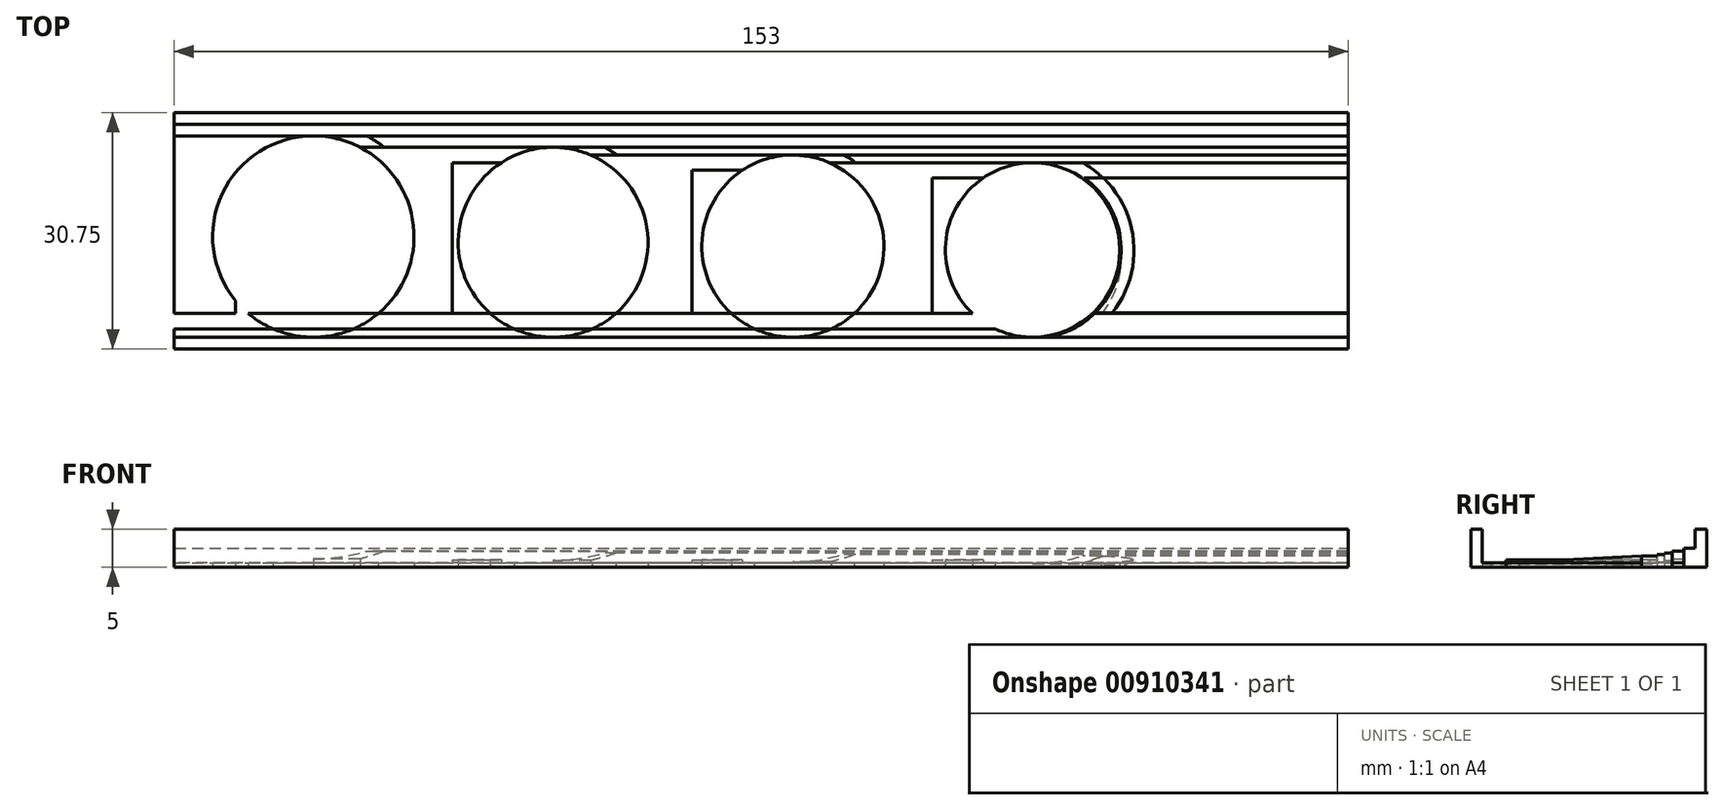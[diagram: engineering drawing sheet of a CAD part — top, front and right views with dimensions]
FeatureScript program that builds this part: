
annotation { "Feature Type Name" : "Feature", "Feature Type Description" : "" }
export const myFeature = defineFeature(function(context is Context, id is Id, definition is map)
    precondition{}
    {
        {
            var Q0;
            Q0=qCreatedBy(makeId("Top.planeOp"),FACE);
            var sketch = newSketch(context, id + "F0", { "sketchPlane" : qUnion([Q0])});
            skLineSegment(sketch, "E0.bottom", {"start": v(0, 0) * mm, "end": v(153, 0) * mm});
            skLineSegment(sketch, "E0.top", {"start": v(0, 29.25) * mm, "end": v(153, 29.25) * mm});
            skLineSegment(sketch, "E0.left", {"start": v(0, 0) * mm, "end": v(0, 29.25) * mm});
            skLineSegment(sketch, "E0.right", {"start": v(153, 0) * mm, "end": v(153, 29.25) * mm});
            skLineSegment(sketch, "E1", {"start": v(5, 0) * mm, "end": v(5, 29.25) * mm, "construction": true});
            skLineSegment(sketch, "E2", {"start": v(31.25, 0) * mm, "end": v(31.25, 29.25) * mm, "construction": true});
            skLineSegment(sketch, "E3", {"start": v(36.25, 29.25) * mm, "end": v(36.25, 0) * mm, "construction": true});
            skLineSegment(sketch, "E4", {"start": v(62.5, 0) * mm, "end": v(62.5, 29.25) * mm, "construction": true});
            skLineSegment(sketch, "E5", {"start": v(67.5, 29.25) * mm, "end": v(67.5, 0) * mm, "construction": true});
            skLineSegment(sketch, "E6", {"start": v(93.75, 29.25) * mm, "end": v(93.75, 0) * mm, "construction": true});
            skLineSegment(sketch, "E7", {"start": v(98.75, 29.25) * mm, "end": v(98.75, 0) * mm, "construction": true});
            skLineSegment(sketch, "E8", {"start": v(125, 29.25) * mm, "end": v(125, 0) * mm, "construction": true});
            skLineSegment(sketch, "E9", {"start": v(0, 1.1) * mm, "end": v(153, 1.1) * mm});
            skLineSegment(sketch, "E10", {"start": v(18.13, 0) * mm, "end": v(18.12, 29.25) * mm, "construction": true});
            skLineSegment(sketch, "E11", {"start": v(49.38, 0) * mm, "end": v(49.37, 29.25) * mm, "construction": true});
            skLineSegment(sketch, "E12", {"start": v(80.62, 29.25) * mm, "end": v(80.62, 0) * mm, "construction": true});
            skLineSegment(sketch, "E13", {"start": v(111.88, 0) * mm, "end": v(111.88, 29.25) * mm, "construction": true});
            skCircle(sketch, "E14", {"center": v(49.37, 12.38) * mm, "radius": 12.38 * mm});
            skCircle(sketch, "E15", {"center": v(80.62, 11.88) * mm, "radius": 11.88 * mm});
            skCircle(sketch, "E16", {"center": v(111.88, 11.38) * mm, "radius": 11.38 * mm});
            skCircle(sketch, "E17", {"center": v(18.12, 13.12) * mm, "radius": 13.12 * mm});
            skLineSegment(sketch, "E18", {"start": v(0, 26.25) * mm, "end": v(153, 26.25) * mm});
            skLineSegment(sketch, "E19", {"start": v(153, 24.75) * mm, "end": v(24.22, 24.75) * mm});
            skLineSegment(sketch, "E20", {"start": v(153, 23.75) * mm, "end": v(54.25, 23.75) * mm});
            skLineSegment(sketch, "E21", {"start": v(153, 22.75) * mm, "end": v(85.4, 22.75) * mm});
            skLineSegment(sketch, "E22", {"start": v(153, 20.75) * mm, "end": v(118.32, 20.75) * mm});
            skLineSegment(sketch, "E23", {"start": v(153, 27.75) * mm, "end": v(0, 27.75) * mm});
            skLineSegment(sketch, "E24", {"start": v(153, 0) * mm, "end": v(153, -1.5) * mm});
            skLineSegment(sketch, "E25", {"start": v(153, -1.5) * mm, "end": v(0, -1.5) * mm});
            skLineSegment(sketch, "E26", {"start": v(0, -1.5) * mm, "end": v(0, 0) * mm});
            skLineSegment(sketch, "E27", {"start": v(0, 3.1) * mm, "end": v(153, 3.1) * mm});
            skLineSegment(sketch, "E28.bottom", {"start": v(3, 3.1) * mm, "end": v(8, 3.1) * mm});
            skLineSegment(sketch, "E28.top", {"start": v(3, 26.25) * mm, "end": v(8, 26.25) * mm});
            skLineSegment(sketch, "E28.left", {"start": v(3, 3.1) * mm, "end": v(3, 26.25) * mm});
            skLineSegment(sketch, "E28.right", {"start": v(8, 3.1) * mm, "end": v(8, 26.25) * mm});
            skLineSegment(sketch, "E29.bottom", {"start": v(36.25, 3.1) * mm, "end": v(42.63, 3.1) * mm});
            skLineSegment(sketch, "E29.top", {"start": v(36.25, 22.75) * mm, "end": v(42.63, 22.75) * mm});
            skLineSegment(sketch, "E29.left", {"start": v(36.25, 3.1) * mm, "end": v(36.25, 22.75) * mm});
            skLineSegment(sketch, "E29.right", {"start": v(42.63, 3.1) * mm, "end": v(42.63, 22.75) * mm});
            skLineSegment(sketch, "E30.bottom", {"start": v(67.5, 3.1) * mm, "end": v(74.03, 3.1) * mm});
            skLineSegment(sketch, "E30.top", {"start": v(67.5, 21.75) * mm, "end": v(74.03, 21.75) * mm});
            skLineSegment(sketch, "E30.left", {"start": v(67.5, 3.1) * mm, "end": v(67.5, 21.75) * mm});
            skLineSegment(sketch, "E30.right", {"start": v(74.03, 3.1) * mm, "end": v(74.03, 21.75) * mm});
            skLineSegment(sketch, "E31.bottom", {"start": v(98.75, 3.1) * mm, "end": v(105.43, 3.1) * mm});
            skLineSegment(sketch, "E31.top", {"start": v(98.75, 20.75) * mm, "end": v(105.43, 20.75) * mm});
            skLineSegment(sketch, "E31.left", {"start": v(98.75, 3.1) * mm, "end": v(98.75, 20.75) * mm});
            skLineSegment(sketch, "E31.right", {"start": v(105.43, 3.1) * mm, "end": v(105.43, 20.75) * mm});
            skSolve(sketch);
        }
        {
            var Q0;
            {var subQ0=sQuery(id+"F0.wireOp",EDGE,"E14");var subQ1=sQuery(id+"F0.wireOp",EDGE,"E0.bottom");var subQ2=makeQuery(id+"F0.imprint","INTERSECT",VERTEX,{"derivedFrom":[subQ1,subQ0]});Q0=makeQuery(id+"F0.imprint","IMPRINT",FACE,{"disambiguationData":[TD([[makeQuery(id+"F0.imprint","IMPRINT",EDGE,{"disambiguationData":[TD([[subQ2,-1.0]])],"derivedFrom":subQ1}),1.0]])]});}
            var Q1;
            {var subQ0=sQuery(id+"F0.wireOp",EDGE,"E0.right");var subQ5=sQuery(id+"F0.wireOp",EDGE,"E9");var subQ6=makeQuery(id+"F0.imprint","INTERSECT",VERTEX,{"derivedFrom":[subQ0,subQ5]});Q1=makeQuery(id+"F0.imprint","IMPRINT",FACE,{"disambiguationData":[TD([[makeQuery(id+"F0.imprint","IMPRINT",EDGE,{"disambiguationData":[TD([[subQ6,1.0]])],"derivedFrom":subQ5}),-1.0]])]});}
            var Q2;
            {var subQ0=sQuery(id+"F0.wireOp",EDGE,"E17");var subQ1=sQuery(id+"F0.wireOp",EDGE,"E9");var subQ2=makeQuery(id+"F0.imprint","INTERSECT",VERTEX,{"disambiguationData":[OD(0.0)],"derivedFrom":[subQ1,subQ0]});Q2=makeQuery(id+"F0.imprint","IMPRINT",FACE,{"disambiguationData":[TD([[makeQuery(id+"F0.imprint","IMPRINT",EDGE,{"disambiguationData":[TD([[subQ2,-1.0]])],"derivedFrom":subQ1}),-1.0]])]});}
            var Q3;
            {var subQ0=sQuery(id+"F0.wireOp",EDGE,"E31.top");Q3=makeQuery(id+"F0.imprint","IMPRINT",FACE,{"disambiguationData":[TD([[makeQuery(id+"F0.imprint","IMPRINT",EDGE,{"derivedFrom":subQ0}),-1.0]])]});}
            var Q4;
            {var subQ1=sQuery(id+"F0.wireOp",EDGE,"E0.right");var subQ4=sQuery(id+"F0.wireOp",EDGE,"E20");var subQ5=makeQuery(id+"F0.imprint","INTERSECT",VERTEX,{"derivedFrom":[subQ1,subQ4]});Q4=makeQuery(id+"F0.imprint","IMPRINT",FACE,{"disambiguationData":[TD([[makeQuery(id+"F0.imprint","IMPRINT",EDGE,{"disambiguationData":[TD([[subQ5,1.0]])],"derivedFrom":subQ1}),1.0]])]});}
            var Q5;
            {var subQ1=sQuery(id+"F0.wireOp",EDGE,"E0.right");var subQ4=sQuery(id+"F0.wireOp",EDGE,"E19");var subQ5=makeQuery(id+"F0.imprint","INTERSECT",VERTEX,{"derivedFrom":[subQ1,subQ4]});Q5=makeQuery(id+"F0.imprint","IMPRINT",FACE,{"disambiguationData":[TD([[makeQuery(id+"F0.imprint","IMPRINT",EDGE,{"disambiguationData":[TD([[subQ5,1.0]])],"derivedFrom":subQ1}),1.0]])]});}
            var Q6;
            {var subQ0=sQuery(id+"F0.wireOp",EDGE,"E30.top");Q6=makeQuery(id+"F0.imprint","IMPRINT",FACE,{"disambiguationData":[TD([[makeQuery(id+"F0.imprint","IMPRINT",EDGE,{"derivedFrom":subQ0}),-1.0]])]});}
            var Q7;
            {var subQ3=sQuery(id+"F0.wireOp",EDGE,"E17");var subQ5=sQuery(id+"F0.wireOp",EDGE,"E9");var subQ6=makeQuery(id+"F0.imprint","INTERSECT",VERTEX,{"disambiguationData":[OD(1.0)],"derivedFrom":[subQ5,subQ3]});Q7=makeQuery(id+"F0.imprint","IMPRINT",FACE,{"disambiguationData":[TD([[makeQuery(id+"F0.imprint","IMPRINT",EDGE,{"disambiguationData":[TD([[subQ6,-1.0]])],"derivedFrom":subQ5}),1.0]])]});}
            var Q8;
            {var subQ5=sQuery(id+"F0.wireOp",EDGE,"E28.bottom");Q8=makeQuery(id+"F0.imprint","IMPRINT",FACE,{"disambiguationData":[TD([[makeQuery(id+"F0.imprint","IMPRINT",EDGE,{"derivedFrom":subQ5}),1.0]])]});}
            var Q9;
            {var subQ0=sQuery(id+"F0.wireOp",EDGE,"E16");var subQ1=sQuery(id+"F0.wireOp",EDGE,"E9");var subQ2=makeQuery(id+"F0.imprint","INTERSECT",VERTEX,{"disambiguationData":[OD(0.0)],"derivedFrom":[subQ1,subQ0]});Q9=makeQuery(id+"F0.imprint","IMPRINT",FACE,{"disambiguationData":[TD([[makeQuery(id+"F0.imprint","IMPRINT",EDGE,{"disambiguationData":[TD([[subQ2,-1.0]])],"derivedFrom":subQ1}),-1.0]])]});}
            var Q10;
            {var subQ6=sQuery(id+"F0.wireOp",EDGE,"E23");Q10=makeQuery(id+"F0.imprint","IMPRINT",FACE,{"disambiguationData":[TD([[makeQuery(id+"F0.imprint","IMPRINT",EDGE,{"derivedFrom":subQ6}),1.0]])]});}
            var Q11;
            {var subQ3=sQuery(id+"F0.wireOp",EDGE,"E22");Q11=makeQuery(id+"F0.imprint","IMPRINT",FACE,{"disambiguationData":[TD([[makeQuery(id+"F0.imprint","IMPRINT",EDGE,{"derivedFrom":subQ3}),-1.0]])]});}
            var Q12;
            {var subQ0=sQuery(id+"F0.wireOp",EDGE,"E22");Q12=makeQuery(id+"F0.imprint","IMPRINT",FACE,{"disambiguationData":[TD([[makeQuery(id+"F0.imprint","IMPRINT",EDGE,{"derivedFrom":subQ0}),1.0]])]});}
            var Q13;
            {var subQ5=sQuery(id+"F0.wireOp",EDGE,"E28.left");Q13=makeQuery(id+"F0.imprint","IMPRINT",FACE,{"disambiguationData":[TD([[makeQuery(id+"F0.imprint","IMPRINT",EDGE,{"derivedFrom":subQ5}),1.0]])]});}
            var Q14;
            {var subQ0=sQuery(id+"F0.wireOp",EDGE,"E0.left");var subQ5=sQuery(id+"F0.wireOp",EDGE,"E9");var subQ6=makeQuery(id+"F0.imprint","INTERSECT",VERTEX,{"derivedFrom":[subQ0,subQ5]});Q14=makeQuery(id+"F0.imprint","IMPRINT",FACE,{"disambiguationData":[TD([[makeQuery(id+"F0.imprint","IMPRINT",EDGE,{"disambiguationData":[TD([[subQ6,-1.0]])],"derivedFrom":subQ5}),-1.0]])]});}
            var Q15;
            {var subQ3=sQuery(id+"F0.wireOp",EDGE,"E14");var subQ6=sQuery(id+"F0.wireOp",EDGE,"E9");var subQ9=makeQuery(id+"F0.imprint","INTERSECT",VERTEX,{"disambiguationData":[OD(1.0)],"derivedFrom":[subQ6,subQ3]});Q15=makeQuery(id+"F0.imprint","IMPRINT",FACE,{"disambiguationData":[TD([[makeQuery(id+"F0.imprint","IMPRINT",EDGE,{"disambiguationData":[TD([[subQ9,-1.0]])],"derivedFrom":subQ6}),1.0]])]});}
            var Q16;
            {var subQ0=sQuery(id+"F0.wireOp",EDGE,"E17");var subQ1=sQuery(id+"F0.wireOp",EDGE,"E0.bottom");var subQ2=makeQuery(id+"F0.imprint","INTERSECT",VERTEX,{"derivedFrom":[subQ1,subQ0]});Q16=makeQuery(id+"F0.imprint","IMPRINT",FACE,{"disambiguationData":[TD([[makeQuery(id+"F0.imprint","IMPRINT",EDGE,{"disambiguationData":[TD([[subQ2,-1.0]])],"derivedFrom":subQ1}),1.0]])]});}
            var Q17;
            {var subQ5=sQuery(id+"F0.wireOp",EDGE,"E30.top");Q17=makeQuery(id+"F0.imprint","IMPRINT",FACE,{"disambiguationData":[TD([[makeQuery(id+"F0.imprint","IMPRINT",EDGE,{"derivedFrom":subQ5}),1.0]])]});}
            var Q18;
            {var subQ8=sQuery(id+"F0.wireOp",EDGE,"E29.top");Q18=makeQuery(id+"F0.imprint","IMPRINT",FACE,{"disambiguationData":[TD([[makeQuery(id+"F0.imprint","IMPRINT",EDGE,{"derivedFrom":subQ8}),1.0]])]});}
            var Q19;
            {var subQ8=sQuery(id+"F0.wireOp",EDGE,"E31.top");Q19=makeQuery(id+"F0.imprint","IMPRINT",FACE,{"disambiguationData":[TD([[makeQuery(id+"F0.imprint","IMPRINT",EDGE,{"derivedFrom":subQ8}),1.0]])]});}
            var Q20;
            {var subQ3=sQuery(id+"F0.wireOp",EDGE,"E28.bottom");Q20=makeQuery(id+"F0.imprint","IMPRINT",FACE,{"disambiguationData":[TD([[makeQuery(id+"F0.imprint","IMPRINT",EDGE,{"derivedFrom":subQ3}),-1.0]])]});}
            var Q21;
            {var subQ0=sQuery(id+"F0.wireOp",EDGE,"E14");var subQ1=sQuery(id+"F0.wireOp",EDGE,"E9");var subQ2=makeQuery(id+"F0.imprint","INTERSECT",VERTEX,{"disambiguationData":[OD(0.0)],"derivedFrom":[subQ1,subQ0]});Q21=makeQuery(id+"F0.imprint","IMPRINT",FACE,{"disambiguationData":[TD([[makeQuery(id+"F0.imprint","IMPRINT",EDGE,{"disambiguationData":[TD([[subQ2,-1.0]])],"derivedFrom":subQ1}),-1.0]])]});}
            var Q22;
            {var subQ1=sQuery(id+"F0.wireOp",EDGE,"E0.right");var subQ4=sQuery(id+"F0.wireOp",EDGE,"E18");var subQ5=makeQuery(id+"F0.imprint","INTERSECT",VERTEX,{"derivedFrom":[subQ1,subQ4]});Q22=makeQuery(id+"F0.imprint","IMPRINT",FACE,{"disambiguationData":[TD([[makeQuery(id+"F0.imprint","IMPRINT",EDGE,{"disambiguationData":[TD([[subQ5,1.0]])],"derivedFrom":subQ1}),1.0]])]});}
            var Q23;
            {var subQ0=sQuery(id+"F0.wireOp",EDGE,"E9");var subQ1=sQuery(id+"F0.wireOp",EDGE,"E0.right");var subQ2=makeQuery(id+"F0.imprint","INTERSECT",VERTEX,{"derivedFrom":[subQ1,subQ0]});Q23=makeQuery(id+"F0.imprint","IMPRINT",FACE,{"disambiguationData":[TD([[makeQuery(id+"F0.imprint","IMPRINT",EDGE,{"disambiguationData":[TD([[subQ2,-1.0]])],"derivedFrom":subQ1}),1.0]])]});}
            var Q24;
            {var subQ6=sQuery(id+"F0.wireOp",EDGE,"E24");Q24=makeQuery(id+"F0.imprint","IMPRINT",FACE,{"disambiguationData":[TD([[makeQuery(id+"F0.imprint","IMPRINT",EDGE,{"derivedFrom":subQ6}),-1.0]])]});}
            var Q25;
            {var subQ3=sQuery(id+"F0.wireOp",EDGE,"E15");var subQ6=sQuery(id+"F0.wireOp",EDGE,"E9");var subQ9=makeQuery(id+"F0.imprint","INTERSECT",VERTEX,{"disambiguationData":[OD(1.0)],"derivedFrom":[subQ6,subQ3]});Q25=makeQuery(id+"F0.imprint","IMPRINT",FACE,{"disambiguationData":[TD([[makeQuery(id+"F0.imprint","IMPRINT",EDGE,{"disambiguationData":[TD([[subQ9,-1.0]])],"derivedFrom":subQ6}),1.0]])]});}
            var Q26;
            {var subQ0=sQuery(id+"F0.wireOp",EDGE,"E0.top");Q26=makeQuery(id+"F0.imprint","IMPRINT",FACE,{"disambiguationData":[TD([[makeQuery(id+"F0.imprint","IMPRINT",EDGE,{"derivedFrom":subQ0}),-1.0]])]});}
            var Q27;
            {var subQ0=sQuery(id+"F0.wireOp",EDGE,"E29.top");Q27=makeQuery(id+"F0.imprint","IMPRINT",FACE,{"disambiguationData":[TD([[makeQuery(id+"F0.imprint","IMPRINT",EDGE,{"derivedFrom":subQ0}),-1.0]])]});}
            var Q28;
            {var subQ0=sQuery(id+"F0.wireOp",EDGE,"E15");var subQ1=sQuery(id+"F0.wireOp",EDGE,"E9");var subQ2=makeQuery(id+"F0.imprint","INTERSECT",VERTEX,{"disambiguationData":[OD(0.0)],"derivedFrom":[subQ1,subQ0]});Q28=makeQuery(id+"F0.imprint","IMPRINT",FACE,{"disambiguationData":[TD([[makeQuery(id+"F0.imprint","IMPRINT",EDGE,{"disambiguationData":[TD([[subQ2,-1.0]])],"derivedFrom":subQ1}),-1.0]])]});}
            var Q29;
            {var subQ0=sQuery(id+"F0.wireOp",EDGE,"E18");var subQ1=sQuery(id+"F0.wireOp",EDGE,"E17");var subQ2=makeQuery(id+"F0.imprint","INTERSECT",VERTEX,{"derivedFrom":[subQ1,subQ0]});Q29=makeQuery(id+"F0.imprint","IMPRINT",FACE,{"disambiguationData":[TD([[makeQuery(id+"F0.imprint","IMPRINT",EDGE,{"disambiguationData":[TD([[subQ2,-1.0]])],"derivedFrom":subQ1}),-1.0]])]});}
            var Q30;
            {var subQ0=sQuery(id+"F0.wireOp",EDGE,"E15");var subQ1=sQuery(id+"F0.wireOp",EDGE,"E0.bottom");var subQ2=makeQuery(id+"F0.imprint","INTERSECT",VERTEX,{"derivedFrom":[subQ1,subQ0]});Q30=makeQuery(id+"F0.imprint","IMPRINT",FACE,{"disambiguationData":[TD([[makeQuery(id+"F0.imprint","IMPRINT",EDGE,{"disambiguationData":[TD([[subQ2,-1.0]])],"derivedFrom":subQ1}),1.0]])]});}
            var Q31;
            {var subQ0=sQuery(id+"F0.wireOp",EDGE,"E28.right");var subQ1=sQuery(id+"F0.wireOp",EDGE,"E17");var subQ2=makeQuery(id+"F0.imprint","INTERSECT",VERTEX,{"disambiguationData":[OD(1.0)],"derivedFrom":[subQ1,subQ0]});Q31=makeQuery(id+"F0.imprint","IMPRINT",FACE,{"disambiguationData":[TD([[makeQuery(id+"F0.imprint","IMPRINT",EDGE,{"disambiguationData":[TD([[subQ2,-1.0]])],"derivedFrom":subQ1}),-1.0]])]});}
            extrude(context, id + "F1", {"entities" : qUnion([Q0, Q1, Q2, Q3, Q4, Q5, Q6, Q7, Q8, Q9, Q10, Q11, Q12, Q13, Q14, Q15, Q16, Q17, Q18, Q19, Q20, Q21, Q22, Q23, Q24, Q25, Q26, Q27, Q28, Q29, Q30, Q31]), "depth" : 0.6 * mm, "offsetDistance" : 25 * mm});
        }
        {
            var Q0;
            {var subQ6=sQuery(id+"F0.wireOp",EDGE,"E23");Q0=makeQuery(id+"F0.imprint","IMPRINT",FACE,{"disambiguationData":[TD([[makeQuery(id+"F0.imprint","IMPRINT",EDGE,{"derivedFrom":subQ6}),1.0]])]});}
            extrude(context, id + "F2", {"entities" : qUnion([Q0]), "depth" : 2.5 * mm, "offsetDistance" : 25 * mm});
        }
        {
            var Q0;
            {var subQ1=sQuery(id+"F0.wireOp",EDGE,"E0.right");var subQ4=sQuery(id+"F0.wireOp",EDGE,"E18");var subQ5=makeQuery(id+"F0.imprint","INTERSECT",VERTEX,{"derivedFrom":[subQ1,subQ4]});Q0=makeQuery(id+"F0.imprint","IMPRINT",FACE,{"disambiguationData":[TD([[makeQuery(id+"F0.imprint","IMPRINT",EDGE,{"disambiguationData":[TD([[subQ5,1.0]])],"derivedFrom":subQ1}),1.0]])]});}
            extrude(context, id + "F3", {"entities" : qUnion([Q0]), "depth" : 2.1 * mm, "offsetDistance" : 25 * mm});
        }
        {
            var Q0;
            {var subQ1=sQuery(id+"F0.wireOp",EDGE,"E0.right");var subQ4=sQuery(id+"F0.wireOp",EDGE,"E19");var subQ5=makeQuery(id+"F0.imprint","INTERSECT",VERTEX,{"derivedFrom":[subQ1,subQ4]});Q0=makeQuery(id+"F0.imprint","IMPRINT",FACE,{"disambiguationData":[TD([[makeQuery(id+"F0.imprint","IMPRINT",EDGE,{"disambiguationData":[TD([[subQ5,1.0]])],"derivedFrom":subQ1}),1.0]])]});}
            extrude(context, id + "F4", {"entities" : qUnion([Q0]), "depth" : 1.9 * mm, "offsetDistance" : 25 * mm});
        }
        {
            var Q0;
            {var subQ1=sQuery(id+"F0.wireOp",EDGE,"E0.right");var subQ4=sQuery(id+"F0.wireOp",EDGE,"E20");var subQ5=makeQuery(id+"F0.imprint","INTERSECT",VERTEX,{"derivedFrom":[subQ1,subQ4]});Q0=makeQuery(id+"F0.imprint","IMPRINT",FACE,{"disambiguationData":[TD([[makeQuery(id+"F0.imprint","IMPRINT",EDGE,{"disambiguationData":[TD([[subQ5,1.0]])],"derivedFrom":subQ1}),1.0]])]});}
            extrude(context, id + "F5", {"entities" : qUnion([Q0]), "operationType" : NewBodyOperationType.ADD, "depth" : 1.7 * mm, "offsetDistance" : 25 * mm});
        }
        {
            var Q0;
            {var subQ3=sQuery(id+"F0.wireOp",EDGE,"E22");Q0=makeQuery(id+"F0.imprint","IMPRINT",FACE,{"disambiguationData":[TD([[makeQuery(id+"F0.imprint","IMPRINT",EDGE,{"derivedFrom":subQ3}),-1.0]])]});}
            extrude(context, id + "F6", {"entities" : qUnion([Q0]), "operationType" : NewBodyOperationType.ADD, "depth" : 1.5 * mm, "offsetDistance" : 25 * mm});
        }
        {
            var Q0;
            {var subQ5=sQuery(id+"F0.wireOp",EDGE,"E28.bottom");Q0=makeQuery(id+"F0.imprint","IMPRINT",FACE,{"disambiguationData":[TD([[makeQuery(id+"F0.imprint","IMPRINT",EDGE,{"derivedFrom":subQ5}),1.0]])]});}
            var Q1;
            {var subQ0=sQuery(id+"F0.wireOp",EDGE,"E29.top");Q1=makeQuery(id+"F0.imprint","IMPRINT",FACE,{"disambiguationData":[TD([[makeQuery(id+"F0.imprint","IMPRINT",EDGE,{"derivedFrom":subQ0}),-1.0]])]});}
            var Q2;
            {var subQ0=sQuery(id+"F0.wireOp",EDGE,"E30.top");Q2=makeQuery(id+"F0.imprint","IMPRINT",FACE,{"disambiguationData":[TD([[makeQuery(id+"F0.imprint","IMPRINT",EDGE,{"derivedFrom":subQ0}),-1.0]])]});}
            var Q3;
            {var subQ0=sQuery(id+"F0.wireOp",EDGE,"E31.top");Q3=makeQuery(id+"F0.imprint","IMPRINT",FACE,{"disambiguationData":[TD([[makeQuery(id+"F0.imprint","IMPRINT",EDGE,{"derivedFrom":subQ0}),-1.0]])]});}
            extrude(context, id + "F7", {"entities" : qUnion([Q0, Q1, Q2, Q3]), "operationType" : NewBodyOperationType.ADD, "depth" : 1 * mm, "offsetDistance" : 25 * mm});
        }
        {
            var Q0;
            {var subQ6=sQuery(id+"F0.wireOp",EDGE,"E24");Q0=makeQuery(id+"F0.imprint","IMPRINT",FACE,{"disambiguationData":[TD([[makeQuery(id+"F0.imprint","IMPRINT",EDGE,{"derivedFrom":subQ6}),-1.0]])]});}
            var Q1;
            {var subQ0=sQuery(id+"F0.wireOp",EDGE,"E0.top");Q1=makeQuery(id+"F0.imprint","IMPRINT",FACE,{"disambiguationData":[TD([[makeQuery(id+"F0.imprint","IMPRINT",EDGE,{"derivedFrom":subQ0}),-1.0]])]});}
            extrude(context, id + "F8", {"entities" : qUnion([Q0, Q1]), "operationType" : NewBodyOperationType.ADD, "depth" : 5 * mm, "offsetDistance" : 25 * mm});
        }
        {
            var Q0;
            {var subQ0=sQuery(id+"F0.wireOp",EDGE,"E22");Q0=makeQuery(id+"F0.imprint","IMPRINT",FACE,{"disambiguationData":[TD([[makeQuery(id+"F0.imprint","IMPRINT",EDGE,{"derivedFrom":subQ0}),1.0]])]});}
            extrude(context, id + "F9", {"entities" : qUnion([Q0]), "depth" : 1.5 * mm, "offsetDistance" : 25 * mm});
        }
        {
            var Q0;
            Q0=makeQuery(id+"F9.opExtrude","SWEPT_FACE",FACE,{"disambiguationData":[OSD([sQuery(id+"F0.wireOp",EDGE,"E0.right")])]});
            var sketch = newSketch(context, id + "F10", { "sketchPlane" : qUnion([Q0])});
            skLineSegment(sketch, "E32", {"start": v(20.75, 1.5) * mm, "end": v(3.1, 0.6) * mm});
            skSolve(sketch);
        }
        {
            var Q0;
            {var subQ0=sQuery(id+"F10.wireOp",EDGE,"E32");Q0=makeQuery(id+"F10.imprint","IMPRINT",FACE,{"disambiguationData":[TD([[makeQuery(id+"F10.imprint","IMPRINT",EDGE,{"derivedFrom":subQ0}),-1.0]])]});}
            extrude(context, id + "F11", {"entities" : qUnion([Q0]), "operationType" : NewBodyOperationType.REMOVE, "oppositeDirection" : true, "depth" : 35 * mm, "offsetDistance" : 25 * mm});
        }
        {
            var Q0;
            Q0=makeQuery(id+"F5.opExtrude","CAP_EDGE",EDGE,{"disambiguationData":[OSD([sQuery(id+"F0.wireOp",EDGE,"E15")])],"isStart":false});
            var Q1;
            Q1=makeQuery(id+"F3.opExtrude","CAP_EDGE",EDGE,{"disambiguationData":[OSD([sQuery(id+"F0.wireOp",EDGE,"E17")])],"isStart":false});
            var Q2;
            Q2=makeQuery(id+"F6.opExtrude","CAP_EDGE",EDGE,{"disambiguationData":[OSD([sQuery(id+"F0.wireOp",EDGE,"E16")])],"isStart":false});
            var Q3;
            Q3=makeQuery(id+"F4.opExtrude","CAP_EDGE",EDGE,{"disambiguationData":[OSD([sQuery(id+"F0.wireOp",EDGE,"E14")])],"isStart":false});
            chamfer(context, id + "F12", {"entities" : qUnion([Q0, Q1, Q2, Q3]), "chamferType" : ChamferType.OFFSET_ANGLE, "width" : 1 * mm, "oppositeDirection" : false, "angle" : 60 * degree, "tangentPropagation" : true});
        }
        {
            var Q0;
            Q0=makeQuery(id+"F11.boolean.opBoolean","INTERSECT",EDGE,{"derivedFrom":[makeQuery(id+"F9.opExtrude","SWEPT_FACE",FACE,{"disambiguationData":[OSD([sQuery(id+"F0.wireOp",EDGE,"E16")])]}),makeQuery(id+"F11.opExtrude","SWEPT_FACE",FACE,{"disambiguationData":[OSD([sQuery(id+"F10.wireOp",EDGE,"E32")])]})]});
            chamfer(context, id + "F13", {"entities" : qUnion([Q0]), "chamferType" : ChamferType.OFFSET_ANGLE, "width" : 1.15 * mm, "oppositeDirection" : false, "angle" : 60 * degree, "tangentPropagation" : true});
        }
    });
